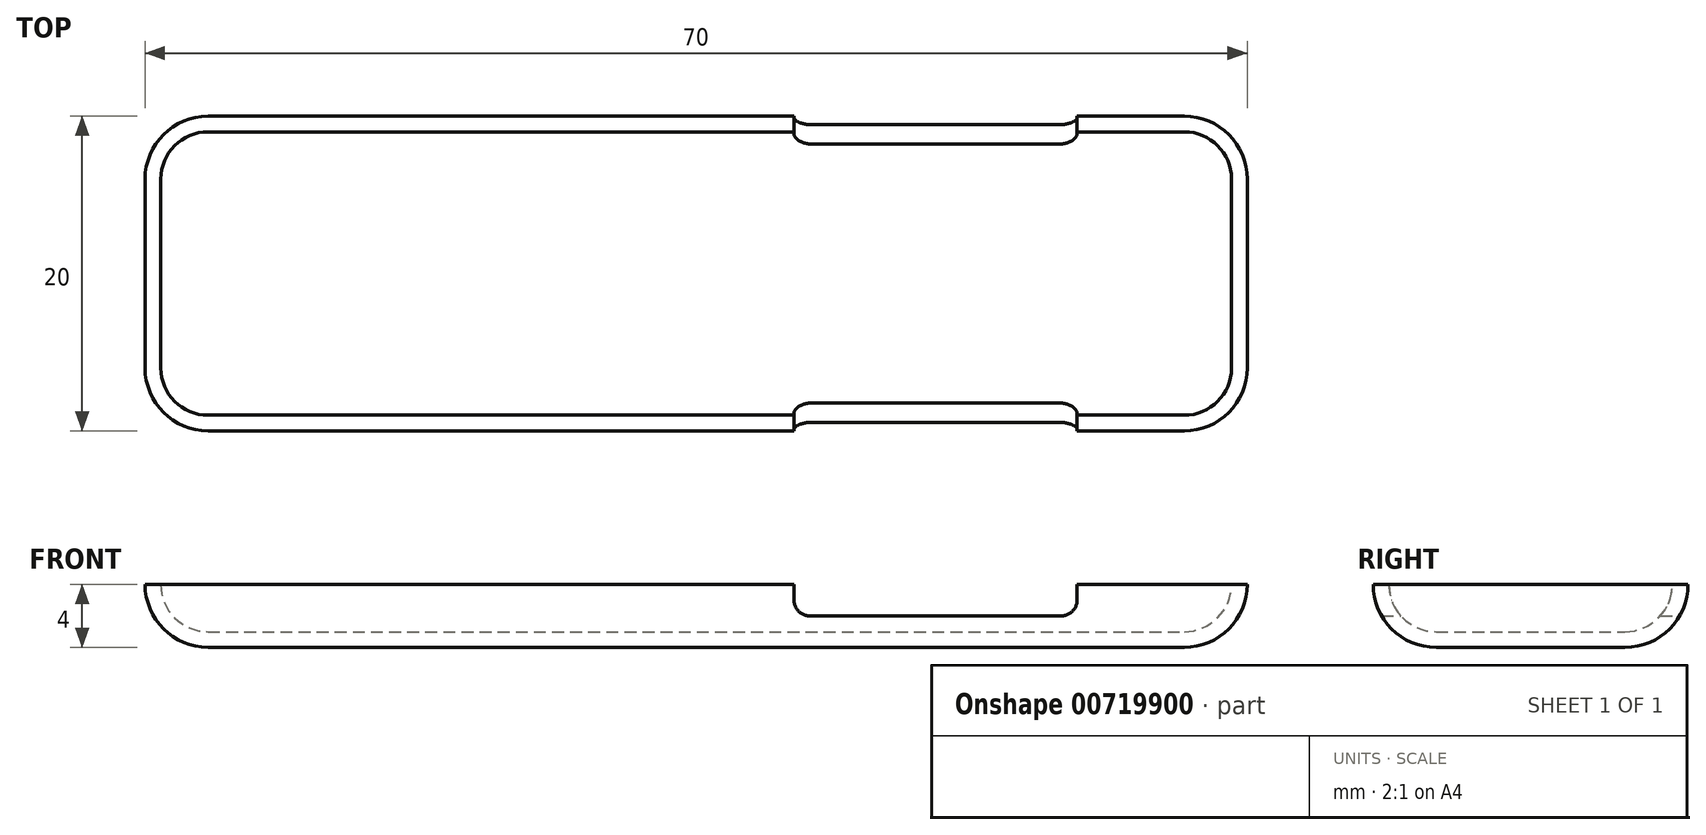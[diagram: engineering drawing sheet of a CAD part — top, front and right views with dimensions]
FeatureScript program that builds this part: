
annotation { "Feature Type Name" : "Feature", "Feature Type Description" : "" }
export const myFeature = defineFeature(function(context is Context, id is Id, definition is map)
    precondition{}
    {
        {
            var Q0;
            Q0=qCreatedBy(makeId("Top.planeOp"),FACE);
            var sketch = newSketch(context, id + "F0", { "sketchPlane" : qUnion([Q0])});
            skLineSegment(sketch, "E0.bottom", {"start": v(35, 10) * mm, "end": v(-35, 10) * mm});
            skLineSegment(sketch, "E0.top", {"start": v(35, -10) * mm, "end": v(-35, -10) * mm});
            skLineSegment(sketch, "E0.left", {"start": v(35, 10) * mm, "end": v(35, -10) * mm});
            skLineSegment(sketch, "E0.right", {"start": v(-35, 10) * mm, "end": v(-35, -10) * mm});
            skPoint(sketch, "E0.middle", {"position": v(0, 0) * mm});
            skSolve(sketch);
        }
        {
            var Q0;
            Q0=makeQuery(id+"F0.imprint","IMPRINT",FACE,{"disambiguationData":[TD([[makeQuery(id+"F0.imprint","IMPRINT",EDGE,{"derivedFrom":sQuery(id+"F0.wireOp",EDGE,"E0.bottom")}),1.0]])]});
            extrude(context, id + "F1", {"entities" : qUnion([Q0]), "depth" : 4 * mm, "offsetDistance" : 25 * mm});
        }
        {
            var Q0;
            Q0=makeQuery(id+"F1.opExtrude","CAP_FACE",FACE,{"disambiguationData":[OSD([sQuery(id+"F0.wireOp",EDGE,"E0.bottom"),sQuery(id+"F0.wireOp",EDGE,"E0.top"),sQuery(id+"F0.wireOp",EDGE,"E0.left"),sQuery(id+"F0.wireOp",EDGE,"E0.right")])],"isStart":true});
            var Q1;
            Q1=makeQuery(id+"F1.opExtrude","SWEPT_EDGE",EDGE,{"disambiguationData":[OSD([sQuery(id+"F0.wireOp",EDGE,"E0.top"),sQuery(id+"F0.wireOp",EDGE,"E0.right")])]});
            var Q2;
            Q2=makeQuery(id+"F1.opExtrude","SWEPT_EDGE",EDGE,{"disambiguationData":[OSD([sQuery(id+"F0.wireOp",EDGE,"E0.bottom"),sQuery(id+"F0.wireOp",EDGE,"E0.right")])]});
            var Q3;
            Q3=makeQuery(id+"F1.opExtrude","SWEPT_EDGE",EDGE,{"disambiguationData":[OSD([sQuery(id+"F0.wireOp",EDGE,"E0.bottom"),sQuery(id+"F0.wireOp",EDGE,"E0.left")])]});
            var Q4;
            Q4=makeQuery(id+"F1.opExtrude","SWEPT_EDGE",EDGE,{"disambiguationData":[OSD([sQuery(id+"F0.wireOp",EDGE,"E0.top"),sQuery(id+"F0.wireOp",EDGE,"E0.left")])]});
            fillet(context, id + "F2", {"entities" : qUnion([Q0, Q1, Q2, Q3, Q4]), "radius" : 4 * mm, "tangentPropagation" : true, "allowEdgeOverflow" : false});
        }
        {
            var Q0;
            Q0=makeQuery(id+"F1.opExtrude","CAP_FACE",FACE,{"disambiguationData":[OSD([sQuery(id+"F0.wireOp",EDGE,"E0.bottom"),sQuery(id+"F0.wireOp",EDGE,"E0.top"),sQuery(id+"F0.wireOp",EDGE,"E0.left"),sQuery(id+"F0.wireOp",EDGE,"E0.right")])],"isStart":false});
            shell(context, id + "F3", {"entities" : qUnion([Q0]), "thickness" : 1 * mm});
        }
        {
            var Q0;
            Q0=makeQuery(id+"F1.opExtrude","CAP_FACE",FACE,{"disambiguationData":[OSD([sQuery(id+"F0.wireOp",EDGE,"E0.bottom"),sQuery(id+"F0.wireOp",EDGE,"E0.top"),sQuery(id+"F0.wireOp",EDGE,"E0.left"),sQuery(id+"F0.wireOp",EDGE,"E0.right")])],"isStart":false});
            var sketch = newSketch(context, id + "F4", { "sketchPlane" : qUnion([Q0])});
            skLineSegment(sketch, "E1.bottom", {"start": v(6.2, -10) * mm, "end": v(24.2, -10) * mm});
            skLineSegment(sketch, "E1.top", {"start": v(6.2, 10) * mm, "end": v(24.2, 10) * mm});
            skLineSegment(sketch, "E1.left", {"start": v(6.2, -10) * mm, "end": v(6.2, 10) * mm});
            skLineSegment(sketch, "E1.right", {"start": v(24.2, -10) * mm, "end": v(24.2, 10) * mm});
            skPoint(sketch, "E1.middle", {"position": v(15.2, 0) * mm});
            skSolve(sketch);
        }
        {
            var Q0;
            Q0 = qSketchRegion(id + "F4", true);
            extrude(context, id + "F5", {"entities" : qUnion([Q0]), "operationType" : NewBodyOperationType.REMOVE, "oppositeDirection" : true, "depth" : 2 * mm, "offsetDistance" : 25 * mm});
        }
        {
            var Q0;
            {var subQ0=sQuery(id+"F0.wireOp",EDGE,"E0.bottom");var subQ1=sQuery(id+"F4.wireOp",EDGE,"E1.right");Q0=makeQuery(id+"F5.boolean.opBoolean","COPY",EDGE,{"disambiguationData":[TD([makeQuery(id+"F2.opFillet","BLEND_FACE",FACE,{"disambiguationData":[OSD([subQ0])]})])],"derivedFrom":makeQuery(id+"F5.opExtrude","CAP_EDGE",EDGE,{"disambiguationData":[OSD([subQ1])],"isStart":false})});}
            var Q1;
            {var subQ0=sQuery(id+"F0.wireOp",EDGE,"E0.bottom");var subQ1=sQuery(id+"F4.wireOp",EDGE,"E1.left");Q1=makeQuery(id+"F5.boolean.opBoolean","COPY",EDGE,{"disambiguationData":[TD([makeQuery(id+"F2.opFillet","BLEND_FACE",FACE,{"disambiguationData":[OSD([subQ0])]})])],"derivedFrom":makeQuery(id+"F5.opExtrude","CAP_EDGE",EDGE,{"disambiguationData":[OSD([subQ1])],"isStart":false})});}
            var Q2;
            {var subQ0=sQuery(id+"F0.wireOp",EDGE,"E0.top");var subQ1=sQuery(id+"F4.wireOp",EDGE,"E1.left");Q2=makeQuery(id+"F5.boolean.opBoolean","COPY",EDGE,{"disambiguationData":[TD([makeQuery(id+"F2.opFillet","BLEND_FACE",FACE,{"disambiguationData":[OSD([subQ0])]})])],"derivedFrom":makeQuery(id+"F5.opExtrude","CAP_EDGE",EDGE,{"disambiguationData":[OSD([subQ1])],"isStart":false})});}
            var Q3;
            {var subQ0=sQuery(id+"F0.wireOp",EDGE,"E0.top");var subQ1=sQuery(id+"F4.wireOp",EDGE,"E1.right");Q3=makeQuery(id+"F5.boolean.opBoolean","COPY",EDGE,{"disambiguationData":[TD([makeQuery(id+"F2.opFillet","BLEND_FACE",FACE,{"disambiguationData":[OSD([subQ0])]})])],"derivedFrom":makeQuery(id+"F5.opExtrude","CAP_EDGE",EDGE,{"disambiguationData":[OSD([subQ1])],"isStart":false})});}
            fillet(context, id + "F6", {"entities" : qUnion([Q0, Q1, Q2, Q3]), "radius" : 1 * mm, "tangentPropagation" : true, "allowEdgeOverflow" : false});
        }
    });
